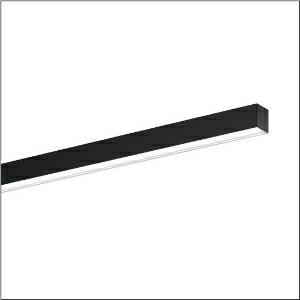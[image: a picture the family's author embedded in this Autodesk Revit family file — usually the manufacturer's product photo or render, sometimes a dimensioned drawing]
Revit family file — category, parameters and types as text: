
# Revit family: silica_r__21_51mx20dc45bb_0fdd
name_source: partatom
category: Lighting Fixtures
units: mm (PartAtom-declared; Revit-internal decimal feet)

## family parameters
Cut with Voids When Loaded = No
Host = Face
Light Source = No
Part Type = Normal
Room Calculation Point = No
Round Connector Dimension = Use Diameter
Shared = No

## types (1)
- --- (1 x LED, 6000 lm, 40.1 W, 4000K)
    Apparent Load = 40 VA
    CIE Flux Codes = 48 79 96 100 100
    Color Rendering = 80
    Color Temperature = 4000K
    Default Elevation = 1800 mm
    Description = Silica® 21, office luminaire, primary optical cover: cover, of PMMA, opal, light emission: direct distribution, primary light characteristic: symmetric, installation type: surface-mounted, LED, rated luminous flux: 6.000lm, luminous efficacy: 150lm/W, light colour: 840, colour temperature: 4000K, control gear: DALI 2, with terminal, 3+2-pole, max. 2.5mm², mains connection: 220..240V, AC, 50/60Hz, rated input power: 40.1W, luminaire housing, of aluminium, matt jet black (RAL 9005), length: 3.004mm, width: 53mm, height: 53mm, protection rating (complete): IP20, insulation class (complete): insulation class I (protective earthing), certification: CE, permissible operating ambient temperature: 0..+35°C, standard: EN 50419, packaging unit: 1 piece
    Height = 53 mm
    Lamp = 1 x LED
    Lamp Light Flux = 6000 lm
    Lamp Power = 40.1 W
    Lamp count = 1
    Length = 3004 mm
    Luminous efficacy = 150 lm/W
    Manufacturer = Siteco
    ModVariant = No
    Model = 51MX20DC45BB
    Mounting Place = Ceiling
    Mounting Type = Surface mounted
    Number of Poles = 1
    OnlyDefault = Yes
    Power Factor = 1
    Product Name = Silica® 21
    Product group = office luminaire | ceiling mounted
    ProductGroupID = 302
    Protection Class = Protection class I
    Protection Degree = IP 20
    RLX_Detail_Level = 1
    RLX_Emergency_Light_Flux = 0 lm
    RLX_Emergency_Type = 0
    RLX_Emergency_Type_DB = No
    RlxData = <blob elided: 28853 chars, md5=4680d5b1>
    Socket = socket
    Standby Power = 0 W
    System Light Flux = 6000 lm
    System Power = 40 W
    Type Comments = factory setting: luminous flux: 100 % | dim-lin: 254 | 218 mA
    Type Image = l_1335925.jpg
    URL = http://relux.com
    VarID = @adj_117844
    Voltage = 0 V
    Weight = 0.00 kg
    Width = 53 mm

## geometry (parser evidence)
native form markers: Blend x4, Sweep x9
no freeform markers — native parametric forms only
